annotation { "Feature Type Name" : "Feature", "Feature Type Description" : "" }
export const myFeature = defineFeature(function(context is Context, id is Id, definition is map)
    precondition{}
    {
        {
            var Q0;
            Q0=qCreatedBy(makeId("Top.planeOp"),FACE);
            var sketch = newSketch(context, id + "F0", { "sketchPlane" : qUnion([Q0])});
            skLineSegment(sketch, "E0.bottom", {"start": v(-39.75, 25.1) * mm, "end": v(39.75, 25.1) * mm});
            skLineSegment(sketch, "E0.top", {"start": v(-39.75, -28.9) * mm, "end": v(39.75, -28.9) * mm});
            skLineSegment(sketch, "E0.left", {"start": v(-42.75, 22.1) * mm, "end": v(-42.75, -25.9) * mm});
            skLineSegment(sketch, "E0.right", {"start": v(42.75, 22.1) * mm, "end": v(42.75, -25.9) * mm});
            skPoint(sketch, "E1.visualSharp", {"position": v(-42.75, 25.1) * mm});
            skArc(sketch, "E1.filletArc", {"start": v(-39.75, 25.1) * mm, "mid": v(-41.87, 24.23) * mm, "end": v(-42.75, 22.1) * mm});
            skPoint(sketch, "E2.visualSharp", {"position": v(42.75, 25.1) * mm});
            skArc(sketch, "E2.filletArc", {"start": v(42.75, 22.1) * mm, "mid": v(41.87, 24.23) * mm, "end": v(39.75, 25.1) * mm});
            skPoint(sketch, "E3.visualSharp", {"position": v(42.75, -28.9) * mm});
            skArc(sketch, "E3.filletArc", {"start": v(39.75, -28.9) * mm, "mid": v(41.87, -28.01) * mm, "end": v(42.75, -25.9) * mm});
            skPoint(sketch, "E4.visualSharp", {"position": v(-42.75, -28.9) * mm});
            skArc(sketch, "E4.filletArc", {"start": v(-42.75, -25.9) * mm, "mid": v(-41.87, -28.01) * mm, "end": v(-39.75, -28.9) * mm});
            skArc(sketch, "E5.0", {"start": v(-39.75, 23.1) * mm, "mid": v(-40.46, 22.81) * mm, "end": v(-40.75, 22.1) * mm});
            skLineSegment(sketch, "E5.1", {"start": v(-39.75, 23.1) * mm, "end": v(39.75, 23.1) * mm});
            skLineSegment(sketch, "E5.2", {"start": v(-40.75, 22.1) * mm, "end": v(-40.75, -25.9) * mm});
            skArc(sketch, "E5.3", {"start": v(40.75, 22.1) * mm, "mid": v(40.46, 22.81) * mm, "end": v(39.75, 23.1) * mm});
            skArc(sketch, "E5.4", {"start": v(-40.75, -25.9) * mm, "mid": v(-40.46, -26.6) * mm, "end": v(-39.75, -26.9) * mm});
            skLineSegment(sketch, "E5.5", {"start": v(-39.75, -26.9) * mm, "end": v(39.75, -26.9) * mm});
            skArc(sketch, "E5.6", {"start": v(39.75, -26.9) * mm, "mid": v(40.46, -26.6) * mm, "end": v(40.75, -25.9) * mm});
            skLineSegment(sketch, "E5.7", {"start": v(40.75, 22.1) * mm, "end": v(40.75, -25.9) * mm});
            skPoint(sketch, "E6", {"position": v(0, 23.1) * mm});
            skSolve(sketch);
        }
        {
            var Q0;
            Q0=qCreatedBy(makeId("Top.planeOp"),FACE);
            var sketch = newSketch(context, id + "F1", { "sketchPlane" : qUnion([Q0])});
            skLineSegment(sketch, "E7.bottom", {"start": v(12.1, 2.5) * mm, "end": v(31.4, 2.5) * mm});
            skLineSegment(sketch, "E7.top", {"start": v(12.1, -23.04) * mm, "end": v(21.75, -23.04) * mm});
            skLineSegment(sketch, "E7.left", {"start": v(9.1, -0.5) * mm, "end": v(9.1, -20.04) * mm});
            skLineSegment(sketch, "E7.right", {"start": v(34.4, -0.5) * mm, "end": v(34.4, -20.04) * mm});
            skPoint(sketch, "E8.visualSharp", {"position": v(9.1, 2.5) * mm});
            skArc(sketch, "E8.filletArc", {"start": v(12.1, 2.5) * mm, "mid": v(9.97, 1.63) * mm, "end": v(9.1, -0.5) * mm});
            skPoint(sketch, "E9.visualSharp", {"position": v(34.4, 2.5) * mm});
            skArc(sketch, "E9.filletArc", {"start": v(34.4, -0.5) * mm, "mid": v(33.53, 1.63) * mm, "end": v(31.4, 2.5) * mm});
            skPoint(sketch, "E10.visualSharp", {"position": v(34.4, -23.04) * mm});
            skArc(sketch, "E10.filletArc", {"start": v(31.4, -23.04) * mm, "mid": v(33.53, -22.16) * mm, "end": v(34.4, -20.04) * mm});
            skPoint(sketch, "E11.visualSharp", {"position": v(9.1, -23.04) * mm});
            skArc(sketch, "E11.filletArc", {"start": v(9.1, -20.04) * mm, "mid": v(9.97, -22.16) * mm, "end": v(12.1, -23.04) * mm});
            skLineSegment(sketch, "E12", {"start": v(21.75, -23.04) * mm, "end": v(21.75, -14.06) * mm});
            skLineSegment(sketch, "E13", {"start": v(21.75, -14.06) * mm, "end": v(19.13, -14.06) * mm});
            skLineSegment(sketch, "E14", {"start": v(18.83, -13.76) * mm, "end": v(18.83, -10.46) * mm});
            skLineSegment(sketch, "E15", {"start": v(19.13, -10.16) * mm, "end": v(21.75, -10.16) * mm});
            skLineSegment(sketch, "E16", {"start": v(21.75, -10.16) * mm, "end": v(21.75, -5.6) * mm});
            skLineSegment(sketch, "E17", {"start": v(25.25, -2.1) * mm, "end": v(28.87, -2.1) * mm});
            skLineSegment(sketch, "E18", {"start": v(29.17, -2.4) * mm, "end": v(29.17, -5.38) * mm});
            skLineSegment(sketch, "E19", {"start": v(28.87, -5.68) * mm, "end": v(26.58, -5.68) * mm});
            skLineSegment(sketch, "E20", {"start": v(25.58, -6.68) * mm, "end": v(25.58, -10.16) * mm});
            skLineSegment(sketch, "E21", {"start": v(25.58, -10.16) * mm, "end": v(29, -10.16) * mm});
            skLineSegment(sketch, "E22", {"start": v(29.5, -10.74) * mm, "end": v(28.98, -13.73) * mm});
            skLineSegment(sketch, "E23", {"start": v(28.58, -14.06) * mm, "end": v(25.58, -14.06) * mm});
            skLineSegment(sketch, "E24", {"start": v(25.58, -14.06) * mm, "end": v(25.58, -23.04) * mm});
            skLineSegment(sketch, "E25.trimOffspring", {"start": v(25.58, -23.04) * mm, "end": v(31.4, -23.04) * mm});
            skPoint(sketch, "E26.visualSharp", {"position": v(21.75, -2.1) * mm});
            skArc(sketch, "E26.filletArc", {"start": v(25.25, -2.1) * mm, "mid": v(22.78, -3.13) * mm, "end": v(21.75, -5.6) * mm});
            skPoint(sketch, "E27.visualSharp", {"position": v(18.83, -10.16) * mm});
            skArc(sketch, "E27.filletArc", {"start": v(19.13, -10.16) * mm, "mid": v(18.92, -10.25) * mm, "end": v(18.83, -10.46) * mm});
            skPoint(sketch, "E28.visualSharp", {"position": v(18.83, -14.06) * mm});
            skArc(sketch, "E28.filletArc", {"start": v(18.83, -13.76) * mm, "mid": v(18.92, -13.97) * mm, "end": v(19.13, -14.06) * mm});
            skPoint(sketch, "E29.visualSharp", {"position": v(28.92, -14.06) * mm});
            skArc(sketch, "E29.filletArc", {"start": v(28.58, -14.06) * mm, "mid": v(28.84, -13.96) * mm, "end": v(28.98, -13.73) * mm});
            skPoint(sketch, "E30.visualSharp", {"position": v(29.6, -10.16) * mm});
            skArc(sketch, "E30.filletArc", {"start": v(29.5, -10.74) * mm, "mid": v(29.38, -10.34) * mm, "end": v(29, -10.16) * mm});
            skPoint(sketch, "E31.visualSharp", {"position": v(25.58, -5.68) * mm});
            skArc(sketch, "E31.filletArc", {"start": v(26.58, -5.68) * mm, "mid": v(25.88, -5.98) * mm, "end": v(25.58, -6.68) * mm});
            skPoint(sketch, "E32.visualSharp", {"position": v(29.17, -5.68) * mm});
            skArc(sketch, "E32.filletArc", {"start": v(28.87, -5.68) * mm, "mid": v(29.08, -5.6) * mm, "end": v(29.17, -5.38) * mm});
            skPoint(sketch, "E33.visualSharp", {"position": v(29.17, -2.1) * mm});
            skArc(sketch, "E33.filletArc", {"start": v(29.17, -2.4) * mm, "mid": v(29.08, -2.2) * mm, "end": v(28.87, -2.1) * mm});
            skSolve(sketch);
        }
        {
            var Q0;
            Q0=qCreatedBy(makeId("Top.planeOp"),FACE);
            var sketch = newSketch(context, id + "F2", { "sketchPlane" : qUnion([Q0])});
            skLineSegment(sketch, "E34", {"start": v(-21.31, -2.24) * mm, "end": v(-11.63, -2.24) * mm});
            skArc(sketch, "E35.0.startCap", {"start": v(-21.31, -4.74) * mm, "mid": v(-23.81, -2.24) * mm, "end": v(-21.31, 0.26) * mm});
            skArc(sketch, "E35.0.endCap", {"start": v(-11.63, 0.26) * mm, "mid": v(-9.13, -2.24) * mm, "end": v(-11.63, -4.74) * mm});
            skLineSegment(sketch, "E35.0.left", {"start": v(-21.31, 0.26) * mm, "end": v(-11.63, 0.26) * mm});
            skLineSegment(sketch, "E35.0.right", {"start": v(-21.31, -4.74) * mm, "end": v(-11.63, -4.74) * mm});
            skLineSegment(sketch, "E36", {"start": v(-21.31, -2.24) * mm, "end": v(-11.64, -2.24) * mm});
            skPoint(sketch, "E36.endSnap0", {"position": v(-9.13, -2.24) * mm});
            skArc(sketch, "E37.0.startCap", {"start": v(-21.31, -9.74) * mm, "mid": v(-28.81, -2.24) * mm, "end": v(-21.31, 5.26) * mm});
            skArc(sketch, "E37.0.endCap", {"start": v(-11.64, 5.26) * mm, "mid": v(-4.14, -2.24) * mm, "end": v(-11.64, -9.74) * mm});
            skLineSegment(sketch, "E37.0.left", {"start": v(-21.31, 5.26) * mm, "end": v(-11.64, 5.26) * mm});
            skLineSegment(sketch, "E37.0.right", {"start": v(-21.31, -9.74) * mm, "end": v(-11.64, -9.74) * mm});
            skSolve(sketch);
        }
        {
            var Q0;
            Q0=qCreatedBy(makeId("Top.planeOp"),FACE);
            var sketch = newSketch(context, id + "F3", { "sketchPlane" : qUnion([Q0])});
            skText(sketch, "E38", { "text": "Brandon Furtwangler", "fontName": "OpenSans-Bold.ttf"});
            const initialGuessF3  = {"E38": [-0.035, 0.0154, 1, 0, 0.0047]};
            skSetInitialGuess(sketch, initialGuessF3);
            skSolve(sketch);
        }
        {
            var Q0;
            Q0=qCreatedBy(makeId("Top.planeOp"),FACE);
            var sketch = newSketch(context, id + "F4", { "sketchPlane" : qUnion([Q0])});
            skText(sketch, "E39", { "text": "<email>", "fontName": "OpenSans-Regular.ttf"});
            const initialGuessF4  = {"E39": [-0.035, 0.00826, 1, 0, 0.00317]};
            skSetInitialGuess(sketch, initialGuessF4);
            skSolve(sketch);
        }
        {
            var Q0;
            Q0=qCreatedBy(makeId("Top.planeOp"),FACE);
            var sketch = newSketch(context, id + "F5", { "sketchPlane" : qUnion([Q0])});
            skText(sketch, "E40", { "text": "Software Developer", "fontName": "OpenSans-Regular.ttf"});
            const initialGuessF5  = {"E40": [-0.03575, -0.0159, 1, 0, 0.00311]};
            skSetInitialGuess(sketch, initialGuessF5);
            skSolve(sketch);
        }
        {
            var Q0;
            Q0=qCreatedBy(makeId("Top.planeOp"),FACE);
            var sketch = newSketch(context, id + "F6", { "sketchPlane" : qUnion([Q0])});
            skText(sketch, "E41", { "text": "Oculus / Facebook", "fontName": "OpenSans-Regular.ttf"});
            const initialGuessF6  = {"E41": [-0.03575, -0.0219, 1, 0, 0.00335]};
            skSetInitialGuess(sketch, initialGuessF6);
            skSolve(sketch);
        }
        {
            var Q0;
            Q0=makeQuery(id+"F0.imprint","IMPRINT",FACE,{"disambiguationData":[TD([[makeQuery(id+"F0.imprint","IMPRINT",EDGE,{"derivedFrom":sQuery(id+"F0.wireOp",EDGE,"E5.0")}),1.0]])]});
            extrude(context, id + "F7", {"entities" : qUnion([Q0]), "depth" : 0.75 * mm});
        }
        {
            var Q0;
            Q0=makeQuery(id+"F0.imprint","IMPRINT",FACE,{"disambiguationData":[TD([[makeQuery(id+"F0.imprint","IMPRINT",EDGE,{"derivedFrom":sQuery(id+"F0.wireOp",EDGE,"E0.bottom")}),-1.0]])]});
            var Q1;
            Q1=makeQuery(id+"F1.imprint","IMPRINT",FACE,{"disambiguationData":[TD([[makeQuery(id+"F1.imprint","IMPRINT",EDGE,{"derivedFrom":sQuery(id+"F1.wireOp",EDGE,"E7.bottom")}),-1.0]])]});
            var Q2;
            Q2=makeQuery(id+"F2.imprint","IMPRINT",FACE,{"disambiguationData":[TD([[makeQuery(id+"F2.imprint","IMPRINT",EDGE,{"derivedFrom":sQuery(id+"F2.wireOp",EDGE,"E35.0.startCap")}),1.0]])]});
            var Q3;
            Q3=qSketchRegion(id+"F6",true);
            var Q4;
            Q4=qSketchRegion(id+"F4",true);
            var Q5;
            Q5=qSketchRegion(id+"F3",true);
            var Q6;
            Q6=qSketchRegion(id+"F5",true);
            extrude(context, id + "F8", {"entities" : qUnion([Q0, Q1, Q2, Q3, Q4, Q5, Q6]), "operationType" : NewBodyOperationType.ADD, "depth" : 1.5 * mm});
        }
    });